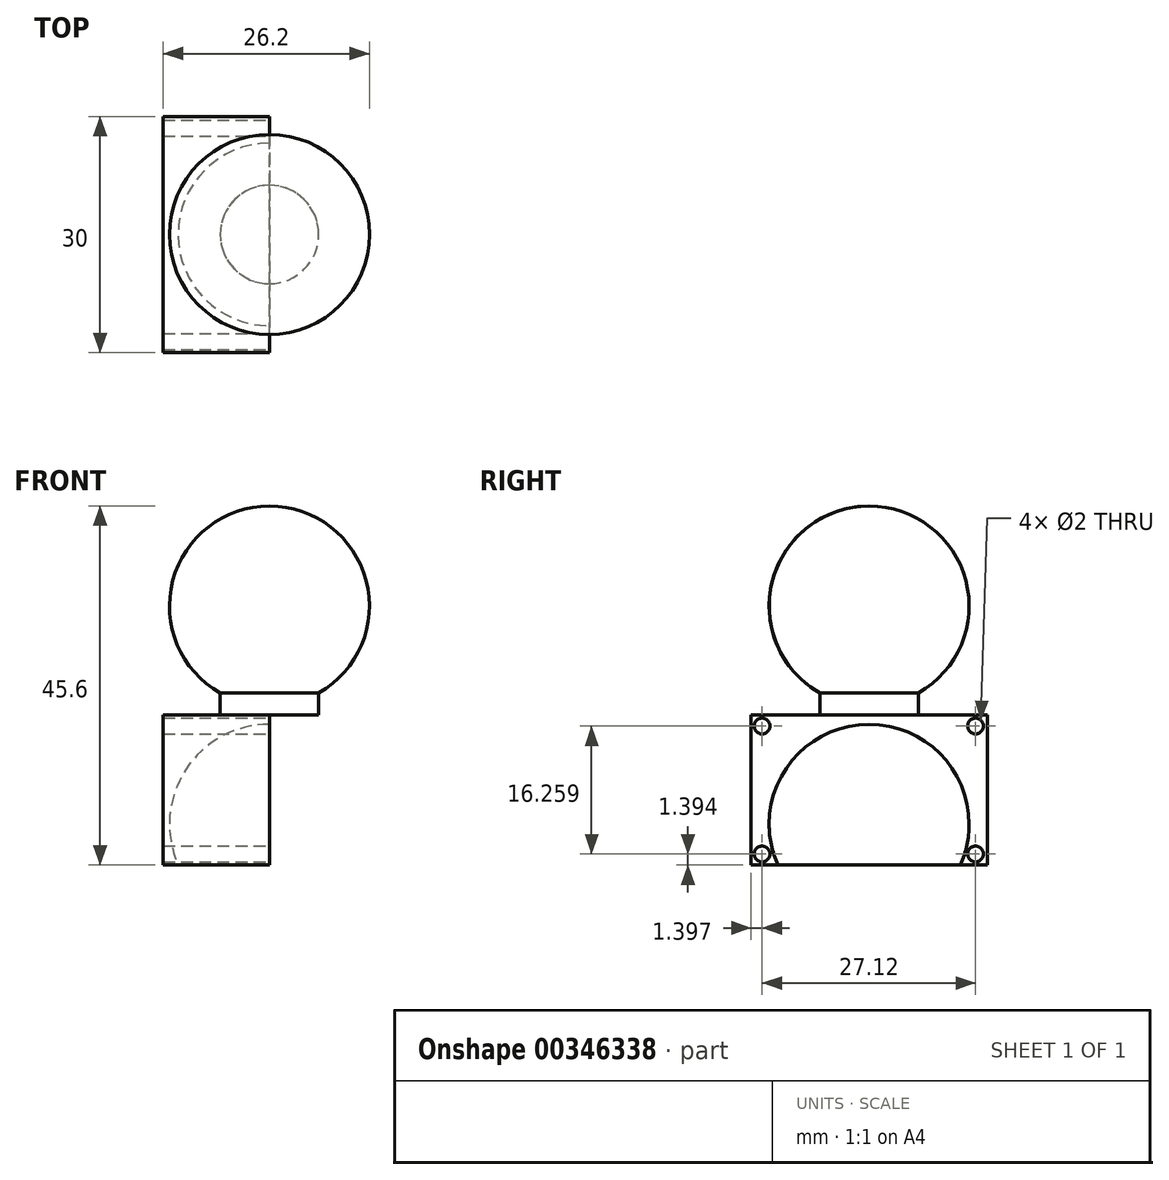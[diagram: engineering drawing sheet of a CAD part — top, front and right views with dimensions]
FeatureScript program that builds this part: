
annotation { "Feature Type Name" : "Feature", "Feature Type Description" : "" }
export const myFeature = defineFeature(function(context is Context, id is Id, definition is map)
    precondition{}
    {
        {
            var Q0;
            Q0=qCreatedBy(makeId("Right.planeOp"),FACE);
            var sketch = newSketch(context, id + "F0", { "sketchPlane" : qUnion([Q0])});
            skCircle(sketch, "E0", {"center": v(0, 13.85) * mm, "radius": 12.7 * mm});
            skLineSegment(sketch, "E1", {"start": v(0, 26.55) * mm, "end": v(0, 1.15) * mm});
            skSolve(sketch);
        }
        {
            var Q0;
            {var subQ0=sQuery(id+"F0.wireOp",EDGE,"E1");Q0=makeQuery(id+"F0.imprint","IMPRINT",FACE,{"disambiguationData":[TD([[makeQuery(id+"F0.imprint","IMPRINT",EDGE,{"derivedFrom":subQ0}),1.0]])]});}
            var Q1;
            Q1 = qConstructionFilter(qBodyType(qCreatedBy(id + "F0" ,EDGE), BodyType.WIRE), ConstructionObject.NO);
            var Q2;
            Q2=sQuery(id+"F0.wireOp",EDGE,"E1");
            revolve(context, id + "F1", {"entities" : qUnion([Q0]), "surfaceEntities" : qUnion([Q1]), "axis" : qUnion([Q2]), "revolveType" : RevolveType.FULL});
        }
        {
            var Q0;
            Q0=qCreatedBy(makeId("Top.planeOp"),FACE);
            var sketch = newSketch(context, id + "F2", { "sketchPlane" : qUnion([Q0])});
            skCircle(sketch, "E2", {"center": v(0, 0) * mm, "radius": 6.26 * mm});
            skSolve(sketch);
        }
        {
            var Q0;
            Q0 = qSketchRegion(id + "F2", true);
            extrude(context, id + "F3", {"entities" : qUnion([Q0]), "operationType" : NewBodyOperationType.ADD, "depth" : 3.05 * mm});
        }
        {
            var Q0;
            Q0=qCreatedBy(makeId("Right.planeOp"),FACE);
            var sketch = newSketch(context, id + "F4", { "sketchPlane" : qUnion([Q0])});
            skLineSegment(sketch, "E3.bottom", {"start": v(-15, 0) * mm, "end": v(15, 0) * mm});
            skLineSegment(sketch, "E3.top", {"start": v(-15, -19.05) * mm, "end": v(15, -19.05) * mm});
            skLineSegment(sketch, "E3.left", {"start": v(-15, 0) * mm, "end": v(-15, -19.05) * mm});
            skLineSegment(sketch, "E3.right", {"start": v(15, 0) * mm, "end": v(15, -19.05) * mm});
            skCircle(sketch, "E4", {"center": v(-13.6, -1.4) * mm, "radius": 1 * mm});
            skCircle(sketch, "E5", {"center": v(13.52, -1.4) * mm, "radius": 1 * mm});
            skCircle(sketch, "E6", {"center": v(13.52, -17.66) * mm, "radius": 1 * mm});
            skCircle(sketch, "E7", {"center": v(-13.6, -17.66) * mm, "radius": 1 * mm});
            skArc(sketch, "E8", {"start": v(11.6, -19.05) * mm, "mid": v(0, -1.17) * mm, "end": v(-11.6, -19.05) * mm});
            skLineSegment(sketch, "E9", {"start": v(-11.6, -19.05) * mm, "end": v(11.6, -19.05) * mm});
            skLineSegment(sketch, "E10", {"start": v(-15, -12.86) * mm, "end": v(-12.66, -12.86) * mm});
            skLineSegment(sketch, "E11", {"start": v(12.66, -12.86) * mm, "end": v(15, -12.86) * mm});
            skLineSegment(sketch, "E12", {"start": v(-12.7, -13.87) * mm, "end": v(12.7, -13.87) * mm});
            skLineSegment(sketch, "E13", {"start": v(0, -13.87) * mm, "end": v(0, -19.05) * mm});
            skLineSegment(sketch, "E14", {"start": v(-13.6, 0) * mm, "end": v(-13.6, -1.4) * mm});
            skLineSegment(sketch, "E15", {"start": v(-15, -1.4) * mm, "end": v(-13.6, -1.4) * mm});
            skSolve(sketch);
        }
        {
            var Q0;
            Q0 = qSketchRegion(id + "F4", true);
            var Q1;
            {var subQ2=sQuery(id+"F4.wireOp",EDGE,"E12");Q1=makeQuery(id+"F4.imprint","IMPRINT",FACE,{"disambiguationData":[TD([[makeQuery(id+"F4.imprint","IMPRINT",EDGE,{"derivedFrom":subQ2}),1.0]])]});}
            extrude(context, id + "F5", {"entities" : qUnion([Q0, Q1]), "operationType" : NewBodyOperationType.ADD, "oppositeDirection" : true, "depth" : 13.5 * mm});
        }
        {
            var Q0;
            {var subQ2=sQuery(id+"F4.wireOp",EDGE,"E12");Q0=makeQuery(id+"F4.imprint","IMPRINT",FACE,{"disambiguationData":[TD([[makeQuery(id+"F4.imprint","IMPRINT",EDGE,{"derivedFrom":subQ2}),1.0]])]});}
            var Q1;
            Q1=sQuery(id+"F4.wireOp",EDGE,"E12");
            var Q2;
            Q2=sQuery(id+"F4.wireOp",EDGE,"E12");
            revolve(context, id + "F6", {"operationType" : NewBodyOperationType.REMOVE, "entities" : qUnion([Q0]), "surfaceEntities" : qUnion([Q1]), "axis" : qUnion([Q2]), "revolveType" : RevolveType.FULL, "oppositeDirection" : true});
        }
    });
